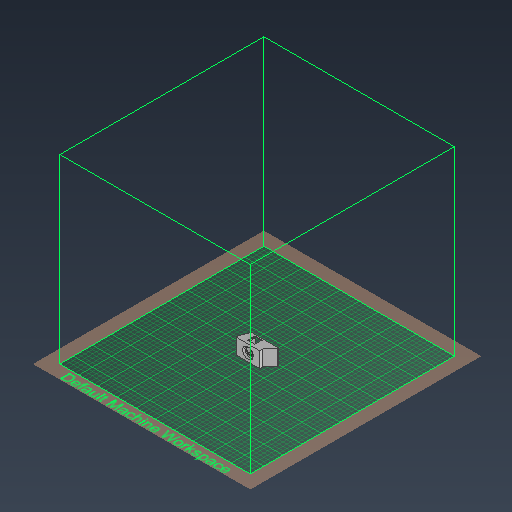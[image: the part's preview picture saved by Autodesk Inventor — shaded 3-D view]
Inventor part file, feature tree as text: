
AUTODESK INVENTOR PART (.ipt)
format: ipt  version: 2021 (Build 250183000, 183)  size: 463,360 bytes
history: native  units: mm
features: extrude x12, sketch x11, other x3, plane x1, loft x1, shell x1
ambient origin geometry x8: Origin, YZ Plane, XZ Plane, XY Plane, X Axis, Y Axis, Z Axis, Center Point
bodies: Volumenkörper1 (feature_tree)
feature tree (29):
  extrude  "Extrusion1"  Depth=34.2mm
  plane  "Arbeitsebene1"
  extrude  "Extrusion2"  Depth=19.0mm
  loft  "Erhebung1"
  shell  "Wandung1"  Thickness=7.3mm
  extrude  "Extrusion5"  TaperAngle=0.0deg  [1 undecoded]
  sketch  "Skizze11"  dims[d8=2.0mm d9=0.0mm d15=0.0mm d16=90.0deg]
  extrude  "Extrusion9"  Depth=2.0mm
  other  "Verdickung1"
  extrude  "Extrusion11"  Depth=4.0mm TaperAngle=0.0deg
  extrude  "Extrusion12"  Depth=21.0mm
  extrude  "Extrusion13"  Depth=1.0mm
  extrude  "Extrusion14"  Depth=6.5mm
  extrude  "Extrusion15"  Depth=21.0mm TaperAngle=0.0deg
  extrude  "Extrusion16"  Depth=10.0mm
  extrude  "Extrusion17"  Depth=10.0mm
  extrude  "Extrusion18"  Depth=5.0mm
  sketch  "Skizze1"  dims[d0=52.0mm d1=34.2mm]
  sketch  "Skizze2"  dims[d2=7.0mm d3=0.0mm d4=19.0mm]
  other  "Kanten1"
  other  "Kanten2"
  sketch  "Skizze7"  dims[d5=60.0mm d6=34.2mm d7=7.3mm]
  sketch  "Skizze13"  dims[d17=0.0mm d18=90.0deg d19=2.0mm]
  sketch  "Skizze14"  dims[d28=2.0mm d29=4.0mm d30=0.0mm]
  sketch  "Skizze15"  dims[d49=6.5mm d50=21.0mm]
  sketch  "Skizze16"  dims[d51=6.0mm d52=0.0mm d56=1.0mm]
  sketch  "Skizze17"  dims[d57=1.0mm d58=6.5mm]
  sketch  "Skizze18"  dims[d59=21.0mm d60=12.0mm d61=0.0mm]
  sketch  "Skizze19"  dims[d65=3.9mm d66=3.25mm d67=3.9mm d68=5.0mm d69=5.0mm d70=3.25mm d71=3.9mm d72=3.25mm d73=5.0mm d74=3.9mm d75=3.25mm d76=5.0mm d77=5.7mm d78=0.0mm d79=6.0mm d80=0.0mm d81=24.2mm d82=5.0mm d83=0.0mm d84=18.0mm d85=5.0mm d86=0.0mm d87=10.5mm d88=8.5mm d95=10.0mm d96=0.0mm d97=3.0mm d98=11.0mm d99=7.0mm d100=18.0mm d101=11.0mm d102=18.0mm d103=10.0mm d104=0.0mm d105=10.0mm d106=0.0mm d31=0.872665mm]
note: 1 required parameter value undecoded (feature->parameter linkage not recoverable at this tier; creation-order binding heuristic only, values carry confidence <= 0.55)
